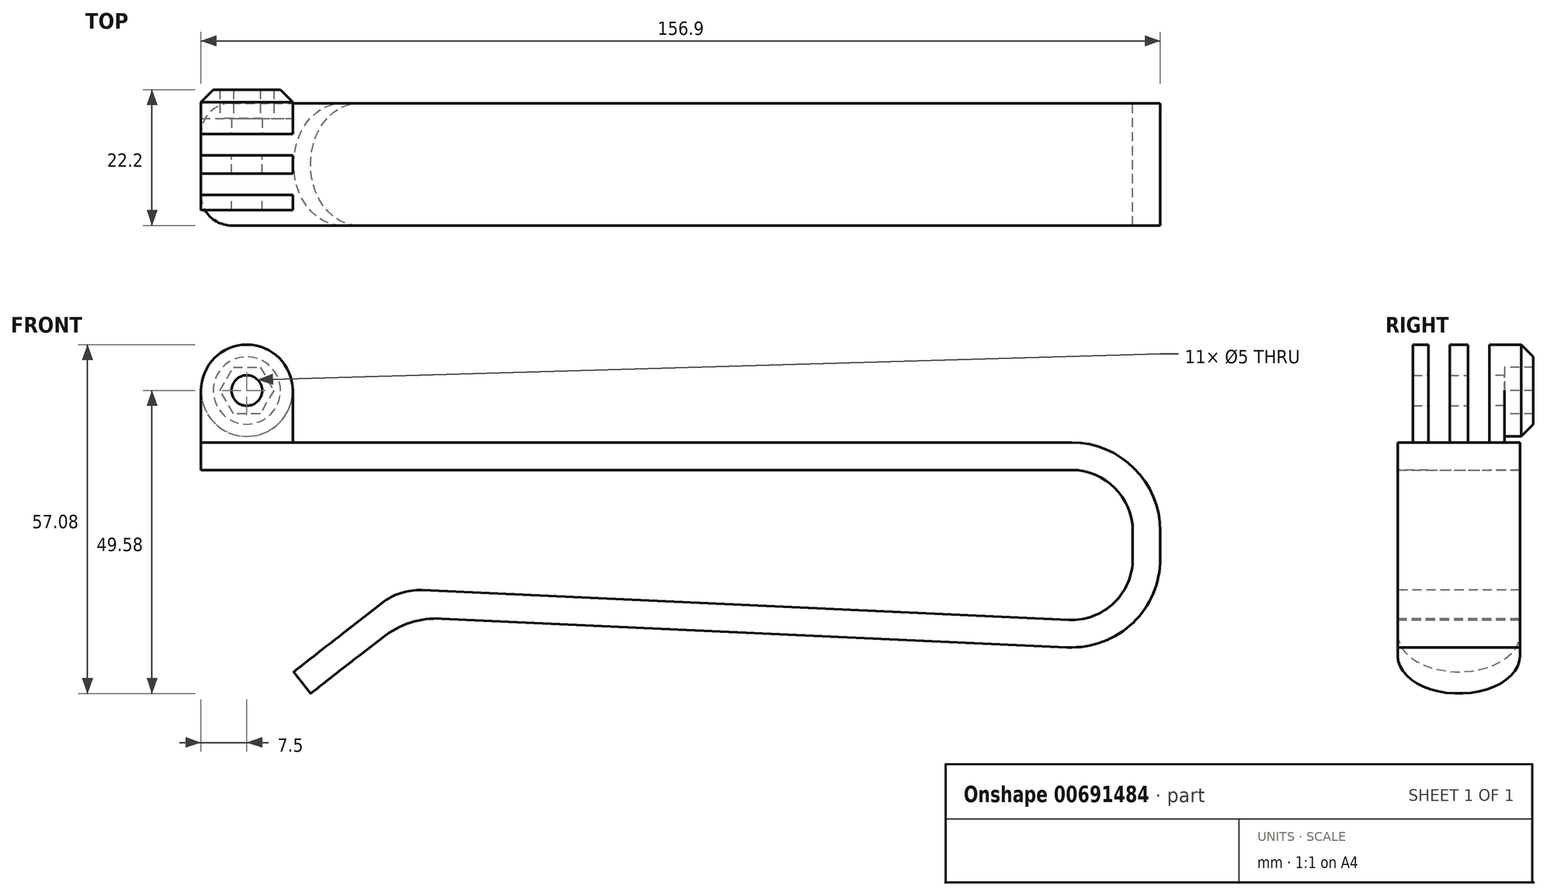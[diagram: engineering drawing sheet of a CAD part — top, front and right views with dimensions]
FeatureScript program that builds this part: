
annotation { "Feature Type Name" : "Feature", "Feature Type Description" : "" }
export const myFeature = defineFeature(function(context is Context, id is Id, definition is map)
    precondition{}
    {
        {
            var Q0;
            Q0=qCreatedBy(makeId("Front.planeOp"),FACE);
            var sketch = newSketch(context, id + "F0", { "sketchPlane" : qUnion([Q0])});
            skCircle(sketch, "E0", {"center": v(0, 0) * mm, "radius": 2.5 * mm});
            skCircle(sketch, "E1", {"center": v(0, 0) * mm, "radius": 7.5 * mm});
            skLineSegment(sketch, "E2", {"start": v(-7.5, 0) * mm, "end": v(-7.5, -8.5) * mm});
            skLineSegment(sketch, "E3", {"start": v(-7.5, -8.5) * mm, "end": v(7.5, -8.5) * mm});
            skLineSegment(sketch, "E4", {"start": v(7.5, 0) * mm, "end": v(7.5, -8.5) * mm});
            skCircle(sketch, "E5.cCircle", {"center": v(0, 0) * mm, "radius": 3.8 * mm, "construction": true});
            skLineSegment(sketch, "E5.0", {"start": v(4.4, 0) * mm, "end": v(2.2, -3.8) * mm});
            skLineSegment(sketch, "E5.1", {"start": v(2.2, -3.8) * mm, "end": v(-2.2, -3.8) * mm});
            skLineSegment(sketch, "E5.2", {"start": v(-2.2, -3.8) * mm, "end": v(-4.4, 0) * mm});
            skLineSegment(sketch, "E5.3", {"start": v(-4.4, 0) * mm, "end": v(-2.2, 3.8) * mm});
            skLineSegment(sketch, "E5.4", {"start": v(-2.2, 3.8) * mm, "end": v(2.2, 3.8) * mm});
            skLineSegment(sketch, "E5.5", {"start": v(2.2, 3.8) * mm, "end": v(4.4, 0) * mm});
            skPoint(sketch, "E5.0.midPoint", {"position": v(3.3, -1.9) * mm});
            skSolve(sketch);
        }
        {
            var Q0;
            {var subQ0=sQuery(id+"F0.wireOp",EDGE,"E2");Q0=makeQuery(id+"F0.imprint","IMPRINT",FACE,{"disambiguationData":[TD([[makeQuery(id+"F0.imprint","IMPRINT",EDGE,{"derivedFrom":subQ0}),1.0]])]});}
            var Q1;
            Q1=makeQuery(id+"F0.imprint","IMPRINT",FACE,{"disambiguationData":[TD([[makeQuery(id+"F0.imprint","IMPRINT",EDGE,{"derivedFrom":sQuery(id+"F0.wireOp",EDGE,"E5.0")}),1.0]])]});
            var Q2;
            Q2=makeQuery(id+"F0.imprint","IMPRINT",FACE,{"disambiguationData":[TD([[makeQuery(id+"F0.imprint","IMPRINT",EDGE,{"derivedFrom":sQuery(id+"F0.wireOp",EDGE,"E0")}),-1.0]])]});
            extrude(context, id + "F1", {"entities" : qUnion([Q0, Q1, Q2]), "endBound" : BoundingType.SYMMETRIC, "depth" : 3 * mm});
        }
        {
            var Q0;
            {var subQ0=sQuery(id+"F0.wireOp",EDGE,"E2");Q0=makeQuery(id+"F0.imprint","IMPRINT",FACE,{"disambiguationData":[TD([[makeQuery(id+"F0.imprint","IMPRINT",EDGE,{"derivedFrom":subQ0}),1.0]])]});}
            var Q1;
            Q1=makeQuery(id+"F0.imprint","IMPRINT",FACE,{"disambiguationData":[TD([[makeQuery(id+"F0.imprint","IMPRINT",EDGE,{"derivedFrom":sQuery(id+"F0.wireOp",EDGE,"E5.0")}),1.0]])]});
            var Q2;
            Q2=makeQuery(id+"F0.imprint","IMPRINT",FACE,{"disambiguationData":[TD([[makeQuery(id+"F0.imprint","IMPRINT",EDGE,{"derivedFrom":sQuery(id+"F0.wireOp",EDGE,"E0")}),-1.0]])]});
            extrude(context, id + "F2", {"entities" : qUnion([Q0, Q1, Q2]), "depth" : 7.5 * mm, "hasSecondDirection" : true, "secondDirectionOppositeDirection" : false, "secondDirectionDepth" : 5 * mm});
        }
        {
            var Q0;
            Q0=makeQuery(id+"F0.imprint","IMPRINT",FACE,{"disambiguationData":[TD([[makeQuery(id+"F0.imprint","IMPRINT",EDGE,{"derivedFrom":sQuery(id+"F0.wireOp",EDGE,"E5.0")}),1.0]])]});
            var Q1;
            {var subQ0=sQuery(id+"F0.wireOp",EDGE,"E2");Q1=makeQuery(id+"F0.imprint","IMPRINT",FACE,{"disambiguationData":[TD([[makeQuery(id+"F0.imprint","IMPRINT",EDGE,{"derivedFrom":subQ0}),1.0]])]});}
            var Q2;
            Q2=makeQuery(id+"F0.imprint","IMPRINT",FACE,{"disambiguationData":[TD([[makeQuery(id+"F0.imprint","IMPRINT",EDGE,{"derivedFrom":sQuery(id+"F0.wireOp",EDGE,"E0")}),-1.0]])]});
            extrude(context, id + "F3", {"entities" : qUnion([Q0, Q1, Q2]), "oppositeDirection" : true, "depth" : 7.5 * mm, "hasSecondDirection" : true, "secondDirectionOppositeDirection" : true, "secondDirectionDepth" : 5 * mm});
        }
        {
            var Q0;
            Q0=makeQuery(id+"F0.imprint","IMPRINT",FACE,{"disambiguationData":[TD([[makeQuery(id+"F0.imprint","IMPRINT",EDGE,{"derivedFrom":sQuery(id+"F0.wireOp",EDGE,"E5.0")}),1.0]])]});
            extrude(context, id + "F4", {"entities" : qUnion([Q0]), "operationType" : NewBodyOperationType.ADD, "oppositeDirection" : true, "depth" : 12.2 * mm, "hasSecondDirection" : true, "secondDirectionOppositeDirection" : true, "secondDirectionDepth" : 7.5 * mm});
        }
        {
            var Q0;
            Q0=makeQuery(id+"F4.opExtrude","CAP_EDGE",EDGE,{"disambiguationData":[OSD([sQuery(id+"F0.wireOp",EDGE,"E1")])],"isStart":false});
            chamfer(context, id + "F5", {"entities" : qUnion([Q0]), "width" : 2 * mm, "tangentPropagation" : true});
        }
        {
            var Q0;
            Q0=qCreatedBy(makeId("Front.planeOp"),FACE);
            var sketch = newSketch(context, id + "F6", { "sketchPlane" : qUnion([Q0])});
            skPoint(sketch, "E6.0", {"position": v(-7.5, -8.5) * mm});
            skLineSegment(sketch, "E7", {"start": v(-7.5, -8.5) * mm, "end": v(149.4, -8.5) * mm});
            skLineSegment(sketch, "E8", {"start": v(149.4, -8.5) * mm, "end": v(149.4, -42.71) * mm});
            skLineSegment(sketch, "E9", {"start": v(-7.5, -8.5) * mm, "end": v(-7.5, -13) * mm});
            skLineSegment(sketch, "E10", {"start": v(-7.5, -13) * mm, "end": v(144.9, -13) * mm});
            skLineSegment(sketch, "E11", {"start": v(144.9, -13) * mm, "end": v(144.9, -38) * mm});
            skPoint(sketch, "E12", {"position": v(25, -32.5) * mm});
            skLineSegment(sketch, "E13", {"start": v(25, -32.5) * mm, "end": v(7.65, -46.03) * mm});
            skLineSegment(sketch, "E14", {"start": v(25, -32.5) * mm, "end": v(144.9, -38) * mm});
            skLineSegment(sketch, "E15.0", {"start": v(26.46, -37.07) * mm, "end": v(10.42, -49.58) * mm});
            skLineSegment(sketch, "E15.1", {"start": v(26.46, -37.07) * mm, "end": v(149.4, -42.71) * mm});
            skLineSegment(sketch, "E16", {"start": v(7.65, -46.03) * mm, "end": v(10.42, -49.58) * mm});
            skSolve(sketch);
        }
        {
            var Q0;
            Q0 = qSketchRegion(id + "F6", true);
            extrude(context, id + "F7", {"entities" : qUnion([Q0]), "endBound" : BoundingType.SYMMETRIC, "depth" : 20 * mm, "offsetDistance" : 25 * mm});
        }
        {
            var Q0;
            Q0=makeQuery(id+"F7.opExtrude","SWEPT_EDGE",EDGE,{"disambiguationData":[OSD([sQuery(id+"F6.wireOp",EDGE,"E13"),sQuery(id+"F6.wireOp",EDGE,"E14")])]});
            var Q1;
            Q1=makeQuery(id+"F7.opExtrude","SWEPT_EDGE",EDGE,{"disambiguationData":[OSD([sQuery(id+"F6.wireOp",EDGE,"E11"),sQuery(id+"F6.wireOp",EDGE,"E14")])]});
            var Q2;
            Q2=makeQuery(id+"F7.opExtrude","SWEPT_EDGE",EDGE,{"disambiguationData":[OSD([sQuery(id+"F6.wireOp",EDGE,"E10"),sQuery(id+"F6.wireOp",EDGE,"E11")])]});
            fillet(context, id + "F8", {"entities" : qUnion([Q0, Q1, Q2]), "radius" : 10 * mm, "tangentPropagation" : true, "allowEdgeOverflow" : false});
        }
        {
            var Q0;
            Q0=makeQuery(id+"F7.opExtrude","SWEPT_EDGE",EDGE,{"disambiguationData":[OSD([sQuery(id+"F6.wireOp",EDGE,"E8"),sQuery(id+"F6.wireOp",EDGE,"E15.1")])]});
            var Q1;
            Q1=makeQuery(id+"F7.opExtrude","SWEPT_EDGE",EDGE,{"disambiguationData":[OSD([sQuery(id+"F6.wireOp",EDGE,"E7"),sQuery(id+"F6.wireOp",EDGE,"E8")])]});
            var Q2;
            Q2=makeQuery(id+"F7.opExtrude","SWEPT_EDGE",EDGE,{"disambiguationData":[OSD([sQuery(id+"F6.wireOp",EDGE,"E15.0"),sQuery(id+"F6.wireOp",EDGE,"E15.1")])]});
            fillet(context, id + "F9", {"entities" : qUnion([Q0, Q1, Q2]), "radius" : (10 + 4.5) * mm, "tangentPropagation" : true, "allowEdgeOverflow" : false});
        }
        {
            var Q0;
            Q0=makeQuery(id+"F7.opExtrude","CAP_EDGE",EDGE,{"disambiguationData":[OSD([sQuery(id+"F6.wireOp",EDGE,"E16")])],"isStart":true});
            var Q1;
            Q1=makeQuery(id+"F7.opExtrude","CAP_EDGE",EDGE,{"disambiguationData":[OSD([sQuery(id+"F6.wireOp",EDGE,"E16")])],"isStart":false});
            fillet(context, id + "F10", {"entities" : qUnion([Q0, Q1]), "radius" : 10 * mm, "tangentPropagation" : true, "allowEdgeOverflow" : false});
        }
        {
            var Q0;
            Q0=makeQuery(id+"F7.opExtrude","CAP_EDGE",EDGE,{"disambiguationData":[OSD([sQuery(id+"F6.wireOp",EDGE,"E9")])],"isStart":false});
            var Q1;
            Q1=makeQuery(id+"F7.opExtrude","CAP_EDGE",EDGE,{"disambiguationData":[OSD([sQuery(id+"F6.wireOp",EDGE,"E9")])],"isStart":true});
            fillet(context, id + "F11", {"entities" : qUnion([Q0, Q1]), "radius" : 5 * mm, "tangentPropagation" : true, "allowEdgeOverflow" : false});
        }
    });
